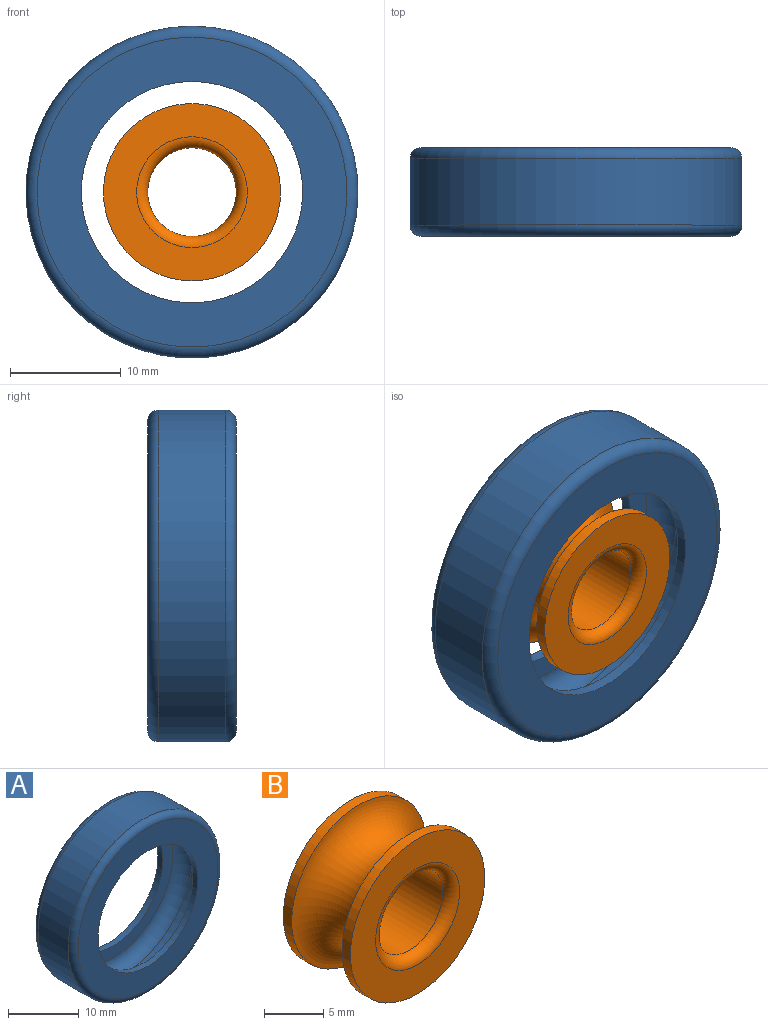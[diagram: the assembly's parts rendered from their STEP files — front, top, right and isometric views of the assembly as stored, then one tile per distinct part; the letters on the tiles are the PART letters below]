
ASSEMBLY  parts=2 mates=1
PART A: 12 faces, bbox 32.5x8x32.5 mm
  f0: plane 28x28mm, normal (0,1,0), area 301.6mm2, adj f1,f11
  f1: torus R=14mm, axis (0,1,0), area 144.5mm2, adj f0,f2
  f2: cylinder r=15mm len=30mm, axis (0,1,0), area 565.5mm2, adj f1,f3
  f3: torus R=14mm, axis (0,1,0), area 144.5mm2, adj f2,f4
  f4: plane 28x28mm, normal (0,-1,0), area 301.6mm2, adj f3,f5
  f5: cylinder r=10mm len=20mm, axis (0,1,0), area 62.8mm2, adj f4,f6
  f6: plane 24x24mm, normal (0,1,0), area 138.2mm2, adj f5,f7
  f7: torus R=12mm, axis (0,1,0), area 262mm2, adj f6,f8
  f8: cylinder r=14mm len=28mm, axis (0,1,0), area 175.9mm2, adj f7,f9
  f9: torus R=12mm, axis (0,1,0), area 262mm2, adj f8,f10
  f10: plane 24x24mm, normal (0,-1,0), area 138.2mm2, adj f9,f11
  f11: cylinder r=10mm len=20mm, axis (0,1,0), area 62.8mm2, adj f0,f10
PART B: 11 faces, bbox 21.9x8x21.9 mm
  f0: cylinder r=4mm len=8mm, axis (0,-1,0), area 150.8mm2, adj f1,f7
  f1: torus R=5mm, axis (0,-1,0), area 43.1mm2, adj f0,f2
  f2: plane 16x16mm, normal (0,1,0), area 122.5mm2, adj f1,f3
  f3: cylinder r=8mm len=16mm, axis (0,-1,0), area 50.3mm2, adj f2,f4
  f4: torus R=8mm, axis (0,-1,0), area 360.6mm2, adj f3,f5
  f5: cylinder r=8mm len=16mm, axis (0,-1,0), area 50.3mm2, adj f4,f6
  f6: plane 16x16mm, normal (0,-1,0), area 122.5mm2, adj f5,f7
  f7: torus R=5mm, axis (0,-1,0), area 43.1mm2, adj f0,f6
  f8: cylinder r=5mm len=10mm, axis (0,-1,0), area 31.4mm2, adj f9,f10
  f9: torus R=5mm, axis (0,-1,0), area 55.6mm2, adj f8,f10
  f10: plane 12x12mm, normal (0,-1,0), area 34.6mm2, adj f8,f9
PLACE A at identity
PLACE B at identity
MATE fastened B.f0 <-> A.f1  axis (0,1,0) through (0,4,0)mm
